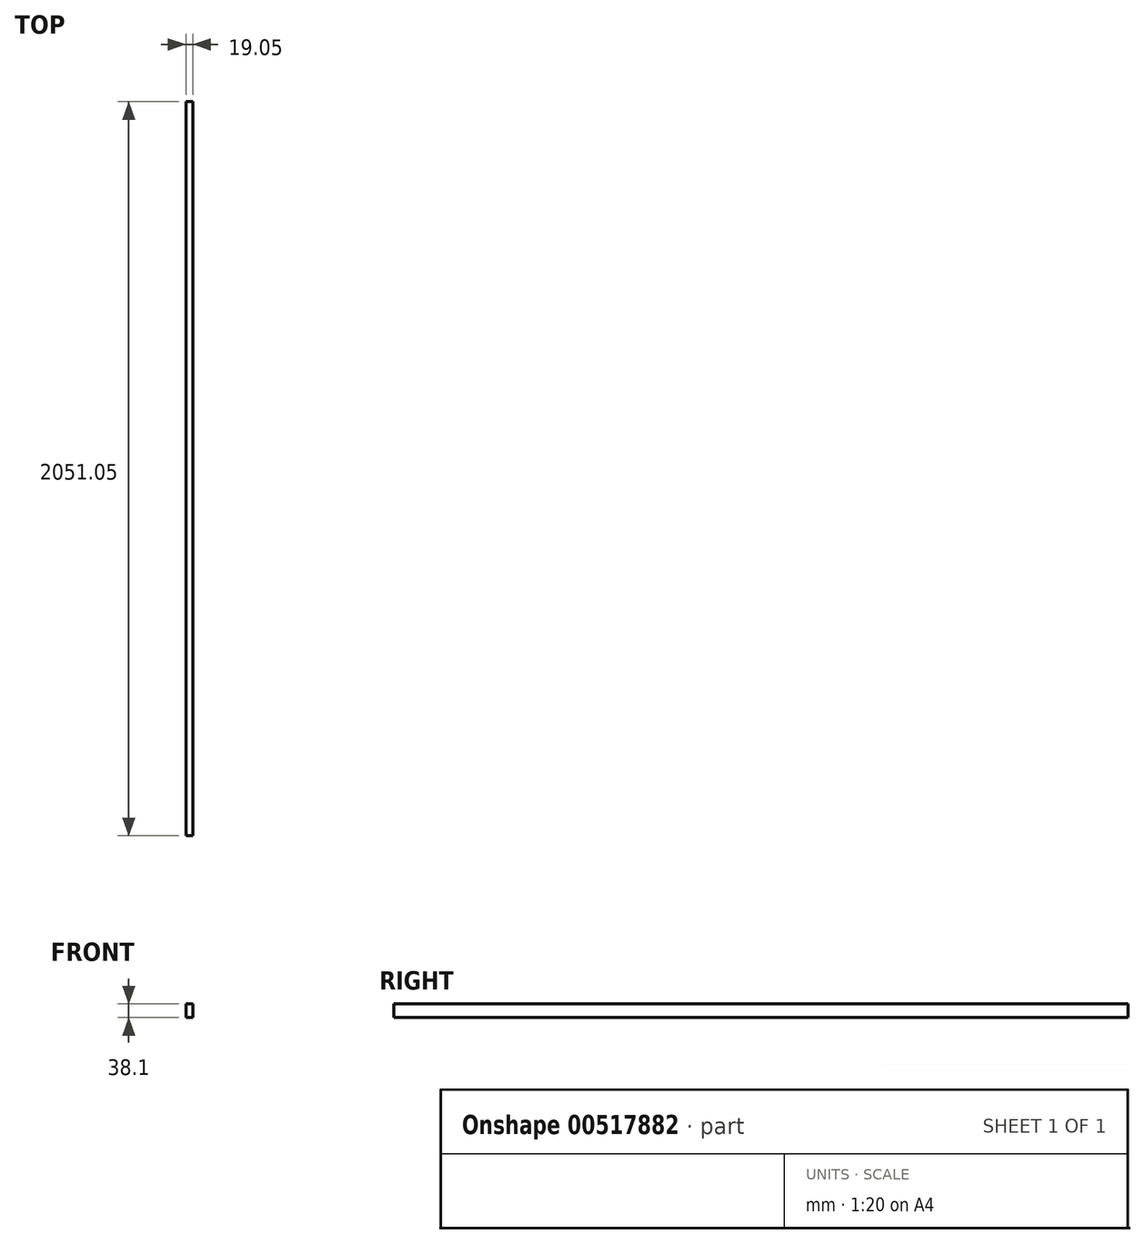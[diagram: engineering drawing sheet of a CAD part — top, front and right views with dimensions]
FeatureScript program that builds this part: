
annotation { "Feature Type Name" : "Feature", "Feature Type Description" : "" }
export const myFeature = defineFeature(function(context is Context, id is Id, definition is map)
    precondition{}
    {
        {
            var Q0;
            Q0=qCreatedBy(makeId("Front.planeOp"),FACE);
            var sketch = newSketch(context, id + "F0", { "sketchPlane" : qUnion([Q0])});
            skLineSegment(sketch, "E0.bottom", {"start": v(0, 0) * mm, "end": v(19.05, 0) * mm});
            skLineSegment(sketch, "E0.top", {"start": v(0, 38.1) * mm, "end": v(19.05, 38.1) * mm});
            skLineSegment(sketch, "E0.left", {"start": v(0, 0) * mm, "end": v(0, 38.1) * mm});
            skLineSegment(sketch, "E0.right", {"start": v(19.05, 0) * mm, "end": v(19.05, 38.1) * mm});
            skLineSegment(sketch, "E1.0", {"start": v(3.17, 34.92) * mm, "end": v(15.87, 34.92) * mm, "construction": true});
            skLineSegment(sketch, "E1.1", {"start": v(3.17, 3.18) * mm, "end": v(3.17, 34.92) * mm, "construction": true});
            skLineSegment(sketch, "E1.2", {"start": v(3.17, 3.18) * mm, "end": v(15.87, 3.18) * mm, "construction": true});
            skLineSegment(sketch, "E1.3", {"start": v(15.87, 3.17) * mm, "end": v(15.87, 34.92) * mm, "construction": true});
            skSolve(sketch);
        }
        {
            var Q0;
            Q0=makeQuery(id+"F0.imprint","IMPRINT",FACE,{"disambiguationData":[TD([[makeQuery(id+"F0.imprint","IMPRINT",EDGE,{"derivedFrom":sQuery(id+"F0.wireOp",EDGE,"E0.bottom")}),1.0]])]});
            extrude(context, id + "F1", {"entities" : qUnion([Q0]), "oppositeDirection" : true, "depth" : 2051.05 * mm, "offsetDistance" : 25.4 * mm});
        }
    });
